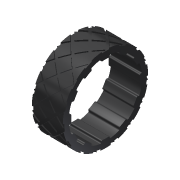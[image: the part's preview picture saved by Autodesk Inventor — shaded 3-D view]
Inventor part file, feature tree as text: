
AUTODESK INVENTOR PART (.ipt)
format: ipt  version: 2013 (Build 170138000, 138)  size: 1,025,536 bytes
history: native  units: in
note: dims shown in document units (in); Inventor stores cm internally (conversion verified against a paired STEP export)
features: extrude x1, mirror x1, imported_body x1, sketch x1
ambient origin geometry x8: Origin, YZ Plane, XZ Plane, XY Plane, X Axis, Y Axis, Z Axis, Center Point
bodies: Solid1 (feature_tree)
feature tree (4):
  extrude  "Extrusion1"  Depth=0.25in TaperAngle=0.0deg
  mirror  "Mirror1"
  imported_body  "Base1"
  sketch  "Sketch1"  dims[d0=4.5in d2=0.25in d3=0.0in]
